# Revit family: Sanitary_Showers_AXOR_29241XXX-AXOR-Bidette-Showers-Bidette-hand-shower-1jet-softsquare-for-cold-water_new
name_source: partatom
category: Plumbing Fixtures
units: mm (PartAtom-declared; Revit-internal decimal feet)

## family parameters
Always vertical = No
Cut with Voids When Loaded = No
Maintain Annotation Orientation = No
OmniClass Number = 23.31.17.00
OmniClass Title = Showers
Part Type = Normal
Room Calculation Point = No
Round Connector Dimension = Use Diameter
Shared = No
Work Plane-Based = Yes

## types (1)
- 29241XXX AXOR Bidette Showers Bidette hand shower 1jet softsquare for cold water with shower holder and hose 1.25 m
    Connector Description = Water Inlet 12.7 mm
    Default Elevation = 1219 mm
    Description = AXOR Bidette Showers Bidette hand shower 1jet softsquare for cold water with shower holder and hose 1.25 m
    Diameter = 13 mm
    Manufacturer = AXOR
    Material 1 = AXOR - Metal - 000 Chrome
    Model = 29241XXX
    Product Page URL = https://www.axor-design.com
    Product data url = https://bimobject.com
    URL = https://www.axor-design.com
    Version = 1

## geometry (parser evidence)
native form markers: Sweep x2
no freeform markers — native parametric forms only
